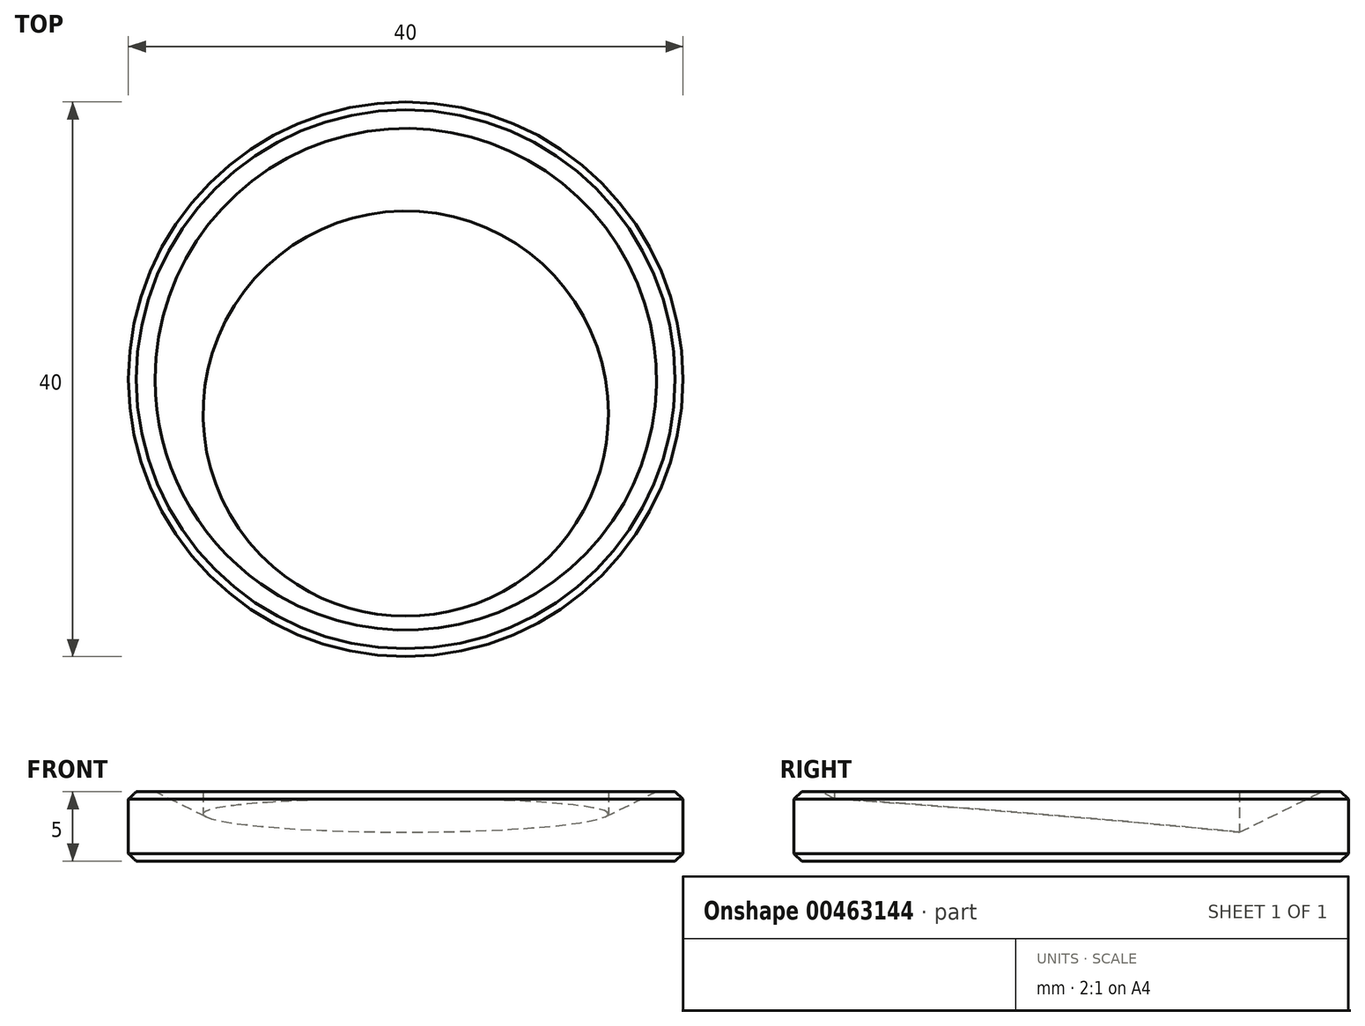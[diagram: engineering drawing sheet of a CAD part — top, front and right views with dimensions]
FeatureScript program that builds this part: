
annotation { "Feature Type Name" : "Feature", "Feature Type Description" : "" }
export const myFeature = defineFeature(function(context is Context, id is Id, definition is map)
    precondition{}
    {
        {
            var Q0;
            Q0=qCreatedBy(makeId("Top.planeOp"),FACE);
            var sketch = newSketch(context, id + "F0", { "sketchPlane" : qUnion([Q0])});
            skCircle(sketch, "E0", {"center": v(0, 0) * mm, "radius": 20 * mm});
            skCircle(sketch, "E1", {"center": v(0, 0) * mm, "radius": 1.5 * mm});
            skSolve(sketch);
        }
        {
            var Q0;
            Q0 = qSketchRegion(id + "F0", true);
            extrude(context, id + "F1", {"entities" : qUnion([Q0]), "depth" : 5 * mm});
        }
        {
            var Q0;
            Q0=qCreatedBy(makeId("Front.planeOp"),FACE);
            var sketch = newSketch(context, id + "F2", { "sketchPlane" : qUnion([Q0])});
            skLineSegment(sketch, "E2", {"start": v(20, 4.46) * mm, "end": v(20, 0.54) * mm});
            skLineSegment(sketch, "E3", {"start": v(19.43, 0) * mm, "end": v(7.89, 0) * mm});
            skLineSegment(sketch, "E4", {"start": v(20, 4.46) * mm, "end": v(19.43, 5) * mm});
            skLineSegment(sketch, "E5", {"start": v(20, 0.54) * mm, "end": v(19.43, 0) * mm});
            skPoint(sketch, "E6", {"position": v(20, 2.5) * mm});
            skLineSegment(sketch, "E7", {"start": v(0, 0) * mm, "end": v(0, 5) * mm});
            skPoint(sketch, "E8", {"position": v(0, 2.5) * mm});
            skLineSegment(sketch, "E9", {"start": v(19.43, 5) * mm, "end": v(18.1, 5) * mm});
            skLineSegment(sketch, "E10", {"start": v(18.1, 5) * mm, "end": v(7.89, 0) * mm});
            skSolve(sketch);
        }
        {
            var Q0;
            Q0 = qSketchRegion(id + "F2", true);
            var Q1;
            Q1=sQuery(id+"F2.wireOp",EDGE,"E7");
            revolve(context, id + "F3", {"operationType" : NewBodyOperationType.INTERSECT, "entities" : qUnion([Q0]), "axis" : qUnion([Q1]), "revolveType" : RevolveType.FULL});
        }
        {
            var Q0;
            Q0=qCreatedBy(makeId("Top.planeOp"),FACE);
            var sketch = newSketch(context, id + "F4", { "sketchPlane" : qUnion([Q0])});
            skCircle(sketch, "E11", {"center": v(0, -2.48) * mm, "radius": 14.61 * mm});
            skSolve(sketch);
        }
        {
            var Q0;
            Q0 = qSketchRegion(id + "F4", true);
            var Q1;
            Q1=makeQuery(id+"F1.opExtrude","CAP_FACE",FACE,{"disambiguationData":[OSD([sQuery(id+"F0.wireOp",EDGE,"E0"),sQuery(id+"F0.wireOp",EDGE,"E1")])],"isStart":false});
            extrude(context, id + "F5", {"entities" : qUnion([Q0]), "operationType" : NewBodyOperationType.ADD, "endBound" : BoundingType.UP_TO_SURFACE, "endBoundEntityFace" : qUnion([Q1]), "depth" : 25 * mm});
        }
    });
